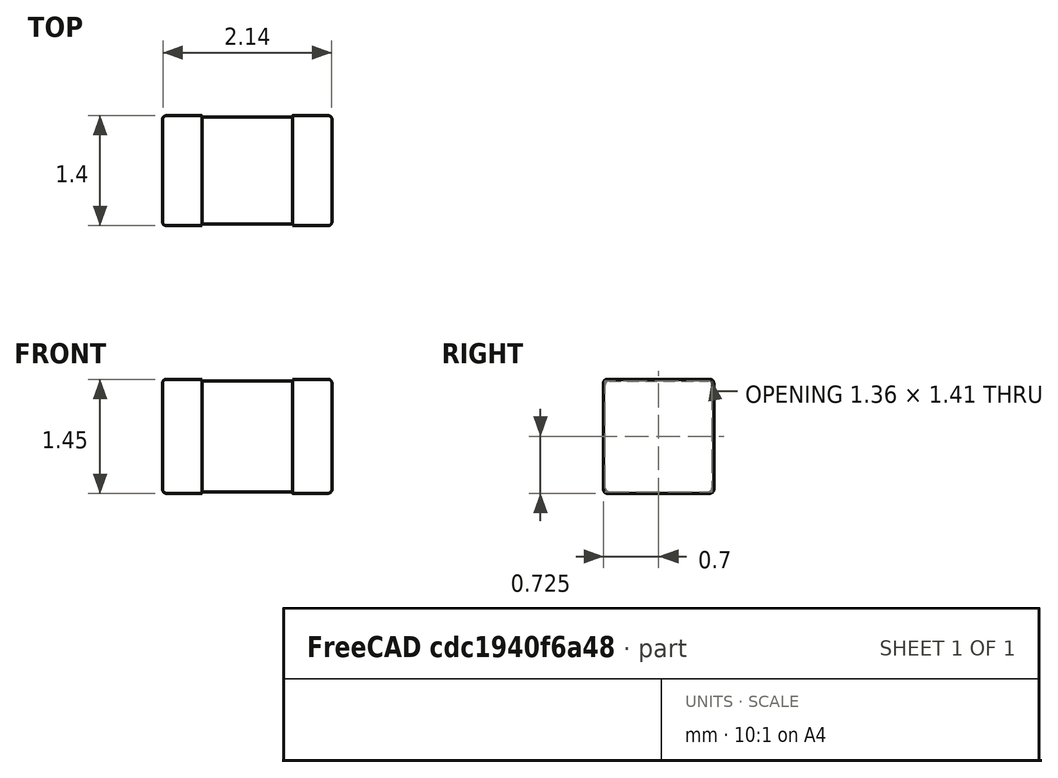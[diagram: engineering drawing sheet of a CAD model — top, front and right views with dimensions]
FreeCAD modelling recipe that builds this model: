
FCSTD DOCUMENT
Label: CAP_CHIP_2012X125
Comment: Kemet C0805... / H1.25+-0.2
objects: Part::Box×3, Part::Fillet×3, Part::MultiFuse×1
note: 7 computed .brp shape members not serialized (recipe doc carries the construction recipe); baked Part::Feature solids carry a one-line shape summary decoded from their .brp

FEATURE [Part::Box] chip
  Height = 1.41
  Length = 2.11
  Placement = pos=(-1.055,-0.68,0.02) rot=(0,0,1;0rad)
  Width = 1.36
FEATURE [Part::Fillet] chip_f
  Base = -> chip
  Edges = 4 edges r=0.05: [Edge9,Edge10,Edge11,Edge12]
FEATURE [Part::Box] plating_left
  Height = 1.45
  Length = 0.5
  Placement = pos=(-1.075,-0.7,0) rot=(0,0,1;0rad)
  Width = 1.4
FEATURE [Part::Fillet] plating_left_f
  Base = -> plating_left
  Edges = 8 edges r=0.05: [Edge1,Edge2,Edge3,Edge4,Edge9,Edge10,Edge11,Edge12]
FEATURE [Part::Box] plating_right
  Height = 1.45
  Length = 0.5
  Placement = pos=(0.575,-0.7,0) rot=(0,0,1;0rad)
  Width = 1.4
FEATURE [Part::Fillet] plating_right_f
  Base = -> plating_right
  Edges = 8 edges r=0.05: [Edge5,Edge6,Edge7,Edge8,Edge9,Edge10,Edge11,Edge12]
FEATURE [Part::MultiFuse] capacitor
  Shapes = -> [chip_f,plating_left_f,plating_right_f]
